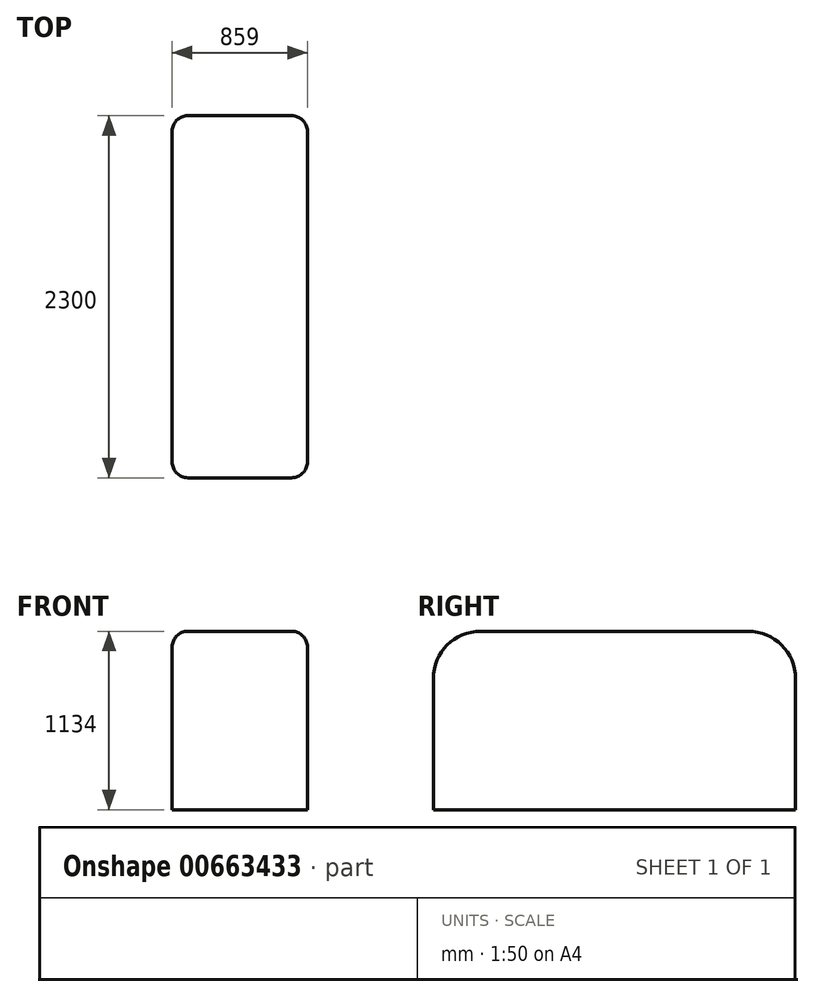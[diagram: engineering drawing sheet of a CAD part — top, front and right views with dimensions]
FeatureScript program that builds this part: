
annotation { "Feature Type Name" : "Feature", "Feature Type Description" : "" }
export const myFeature = defineFeature(function(context is Context, id is Id, definition is map)
    precondition{}
    {
        {
            var Q0;
            Q0=qCreatedBy(makeId("Top.planeOp"),FACE);
            var sketch = newSketch(context, id + "F0", { "sketchPlane" : qUnion([Q0])});
            skLineSegment(sketch, "E0.bottom", {"start": v(-84.39, -56.69) * mm, "end": v(774.61, -56.69) * mm});
            skLineSegment(sketch, "E0.top", {"start": v(-84.39, 2243.31) * mm, "end": v(774.61, 2243.31) * mm});
            skLineSegment(sketch, "E0.left", {"start": v(-84.39, -56.69) * mm, "end": v(-84.39, 2243.31) * mm});
            skLineSegment(sketch, "E0.right", {"start": v(774.61, -56.69) * mm, "end": v(774.61, 2243.31) * mm});
            skSolve(sketch);
        }
        {
            var Q0;
            Q0=makeQuery(id+"F0.imprint","IMPRINT",FACE,{"disambiguationData":[TD([[makeQuery(id+"F0.imprint","IMPRINT",EDGE,{"derivedFrom":sQuery(id+"F0.wireOp",EDGE,"E0.bottom")}),1.0]])]});
            extrude(context, id + "F1", {"entities" : qUnion([Q0]), "depth" : 1134 * mm, "offsetDistance" : 25 * mm});
        }
        {
            var Q0;
            Q0=makeQuery(id+"F1.opExtrude","CAP_EDGE",EDGE,{"disambiguationData":[OSD([sQuery(id+"F0.wireOp",EDGE,"E0.bottom")])],"isStart":false});
            var Q1;
            Q1=makeQuery(id+"F1.opExtrude","CAP_EDGE",EDGE,{"disambiguationData":[OSD([sQuery(id+"F0.wireOp",EDGE,"E0.top")])],"isStart":false});
            fillet(context, id + "F2", {"entities" : qUnion([Q0, Q1]), "radius" : 300 * mm, "tangentPropagation" : true, "allowEdgeOverflow" : false});
        }
        {
            var Q0;
            Q0=makeQuery(id+"F1.opExtrude","CAP_EDGE",EDGE,{"disambiguationData":[OSD([sQuery(id+"F0.wireOp",EDGE,"E0.right")])],"isStart":false});
            var Q1;
            Q1=makeQuery(id+"F2.opFillet","BLEND_EDGE",EDGE,{"blendedFrom":[makeQuery(id+"F1.opExtrude","CAP_EDGE",EDGE,{"disambiguationData":[OSD([sQuery(id+"F0.wireOp",EDGE,"E0.bottom")])],"isStart":false}),makeQuery(id+"F1.opExtrude","SWEPT_FACE",FACE,{"disambiguationData":[OSD([sQuery(id+"F0.wireOp",EDGE,"E0.right")])]})],"blendedInto":[makeQuery(id+"F1.opExtrude","SWEPT_FACE",FACE,{"disambiguationData":[OSD([sQuery(id+"F0.wireOp",EDGE,"E0.right")])]})]});
            var Q2;
            Q2=makeQuery(id+"F1.opExtrude","SWEPT_EDGE",EDGE,{"disambiguationData":[OSD([sQuery(id+"F0.wireOp",EDGE,"E0.bottom"),sQuery(id+"F0.wireOp",EDGE,"E0.right")])]});
            var Q3;
            Q3=makeQuery(id+"F2.opFillet","BLEND_EDGE",EDGE,{"blendedFrom":[makeQuery(id+"F1.opExtrude","CAP_EDGE",EDGE,{"disambiguationData":[OSD([sQuery(id+"F0.wireOp",EDGE,"E0.top")])],"isStart":false}),makeQuery(id+"F1.opExtrude","SWEPT_FACE",FACE,{"disambiguationData":[OSD([sQuery(id+"F0.wireOp",EDGE,"E0.right")])]})],"blendedInto":[makeQuery(id+"F1.opExtrude","SWEPT_FACE",FACE,{"disambiguationData":[OSD([sQuery(id+"F0.wireOp",EDGE,"E0.right")])]})]});
            var Q4;
            Q4=makeQuery(id+"F1.opExtrude","SWEPT_EDGE",EDGE,{"disambiguationData":[OSD([sQuery(id+"F0.wireOp",EDGE,"E0.top"),sQuery(id+"F0.wireOp",EDGE,"E0.right")])]});
            var Q5;
            Q5=makeQuery(id+"F1.opExtrude","SWEPT_EDGE",EDGE,{"disambiguationData":[OSD([sQuery(id+"F0.wireOp",EDGE,"E0.bottom"),sQuery(id+"F0.wireOp",EDGE,"E0.left")])]});
            var Q6;
            Q6=makeQuery(id+"F2.opFillet","BLEND_EDGE",EDGE,{"blendedFrom":[makeQuery(id+"F1.opExtrude","CAP_EDGE",EDGE,{"disambiguationData":[OSD([sQuery(id+"F0.wireOp",EDGE,"E0.bottom")])],"isStart":false}),makeQuery(id+"F1.opExtrude","SWEPT_FACE",FACE,{"disambiguationData":[OSD([sQuery(id+"F0.wireOp",EDGE,"E0.left")])]})],"blendedInto":[makeQuery(id+"F1.opExtrude","SWEPT_FACE",FACE,{"disambiguationData":[OSD([sQuery(id+"F0.wireOp",EDGE,"E0.left")])]})]});
            var Q7;
            Q7=makeQuery(id+"F1.opExtrude","CAP_EDGE",EDGE,{"disambiguationData":[OSD([sQuery(id+"F0.wireOp",EDGE,"E0.left")])],"isStart":false});
            var Q8;
            Q8=makeQuery(id+"F2.opFillet","BLEND_EDGE",EDGE,{"blendedFrom":[makeQuery(id+"F1.opExtrude","CAP_EDGE",EDGE,{"disambiguationData":[OSD([sQuery(id+"F0.wireOp",EDGE,"E0.top")])],"isStart":false}),makeQuery(id+"F1.opExtrude","SWEPT_FACE",FACE,{"disambiguationData":[OSD([sQuery(id+"F0.wireOp",EDGE,"E0.left")])]})],"blendedInto":[makeQuery(id+"F1.opExtrude","SWEPT_FACE",FACE,{"disambiguationData":[OSD([sQuery(id+"F0.wireOp",EDGE,"E0.left")])]})]});
            var Q9;
            Q9=makeQuery(id+"F1.opExtrude","SWEPT_EDGE",EDGE,{"disambiguationData":[OSD([sQuery(id+"F0.wireOp",EDGE,"E0.top"),sQuery(id+"F0.wireOp",EDGE,"E0.left")])]});
            fillet(context, id + "F3", {"entities" : qUnion([Q0, Q1, Q2, Q3, Q4, Q5, Q6, Q7, Q8, Q9]), "radius" : 100 * mm, "tangentPropagation" : true, "allowEdgeOverflow" : false});
        }
    });
